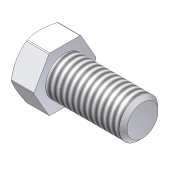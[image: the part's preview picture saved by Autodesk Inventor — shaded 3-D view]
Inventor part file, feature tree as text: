
AUTODESK INVENTOR PART (.ipt)
format: ipt  version: unknown  size: 197,120 bytes
history: native  units: in
note: dims shown in document units (in); Inventor stores cm internally (conversion verified against a paired STEP export)
features: sketch x2, revolve x1, extrude x1, chamfer x1, thread x1
ambient origin geometry x8: Origin, YZ Plane, XZ Plane, XY Plane, X Axis, Y Axis, Z Axis, Center Point
feature tree (6):
  revolve  "Revolution1"  Angle=30.0deg
  extrude  "Extrusion15"  Depth=0.0787in
  chamfer  "Chamfer5"  Angle=90.0deg  [1 undecoded]
  thread  "Thread7"  [1 undecoded]
  sketch  "Sketch15"  dims[d21=0.7874in d83=30.0deg]
  sketch  "Sketch16"  dims[d84=0.1969in d86=0.0787in d92=90.0deg d104=0.5512in d105=0.5906in d106=0.0in d116=0.2756in d117=0.7874in d118=0.0394in d119=0.0787in d120=45.0deg d128=0.1181in d129=1.1811in d130=0.0in]
note: 2 required parameter values undecoded (feature->parameter linkage not recoverable at this tier; creation-order binding heuristic only, values carry confidence <= 0.55)
